# Revit family: O5DMA
name_source: partatom
category: Mechanical Equipment
units: mm (PartAtom-declared; Revit-internal decimal feet)

## family parameters
Always vertical = Yes
Cut with Voids When Loaded = No
OmniClass Number = 23.40.40.11.17
OmniClass Title = Refrigerated Cases
Part Type = Normal
Room Calculation Point = No
Round Connector Dimension = Use Radius
Shared = No
Work Plane-Based = Yes

## types (4) — shared parameters
24" Shelf = Yes
BOTTOM ELECTRICAL = Yes
BOTTOM REFRIGERATION PIPING = Yes
Certifications = NSF 7, UL471, CSA
Condensing  Data Volts = 208 V
Condensing Data  Phase = 1
Condensing Frequency (Hz) = 60 Hz
DATE = 05/20/2016
DESIGNERS NAME = SHIDDRAMESH
DRAIN PIPING = Yes
Default Elevation = 48"
Defrosts Per Day = 6
Description = Multi-Deck Merchandiser
Discharge Air (°F) = 31 °F
Discharge Air Velocity (FPM) = 200 FPM
EQUIPMENT DESCRIPTION = Multi-Deck Merchandiser
EQUIPMENT MARK = O5DMA-NRG
GLASS = Glass
Height = 101 5/8"
Item Description = Multi-Deck Merchandiser
LF STD END = Yes
Legend Number = O5DMA-NRG
Manufacturer = HILL PHOENIX
Model = O5DMA-NRG
PAINTED METAL UPPER SHELF = PAINTED SHELVES
REAR REFRIGERATION PIPING = Yes
RT STD END = Yes
Refrigerant = R404A
Suction Pressure @ Case Outlet (psig) = 58.00 psi
Superheat Set Point @ Bulb (°F) = 6-8  °F
System Data Phase = 1
System Data Volts = 208 V
Systems Frequency = 60 Hz
Systems Wire = 3 wire + ground
TOP ELECTRICAL = Yes
TOP REFRIGERATION PIPING = Yes
Timed-Off Defrost Fail-Safe (Min) = 45 (min)
Timed-Off Defrost Termination Temp = 42 °F
URL = http://www.hillphoenix.com
Width = 43 1/4"

## per-type parameters (varying)
| type | CENTER LINE | Condensed Horsepower | DRAIN LINE | Drain Pump Amps | Drain Pump Watts | Evaporator Pan Heater  Amps | Evaporator Pan Heater  Watts | High Efficiency Amps | High Efficiency Watts | Lbs. of Refrigerant | Length | Length of Cases | Locked Rotor (LRA) Amps | Maximum Lights Amps | Maximum Lights Watts | Number of Fans | Refgn | Running Load (RLA) Amps | Systems Maximum Overcurrent Protection | Systems Minimum Circuit Amps |
| 4' | 24" | 1 | 36" | 1 A | 47 W | 7 A | 1500 W | 0 A | 28 W | 4.5 | 48" | 48" | 46 A | 0 A | 35 W | 2 | 22 1/2" | 10 A | 25 A | 21 A |
| 6' | 36" | 1 - 3/4 | 36" | 1 A | 47 W | 7 A | 1500 W | 0 A | 28 W | 5.2 | 72" | 0" | 55 A | 0 A | 56 W | 2 | 28 5/8" | 13 A | 35 A | 25 A |
| 8' | 48" | 2 | 48" | 1 A | 47 W | 7 A | 1500 W | 0 A | 35 W | 5.2 | 96" | 0" | 56 A | 1 A | 71 W | 2 | 28 5/8" | 12 A | 35 A | 25 A |
| 12' | 72" |  | 72" | 0 A | 0 W | 0 A | 0 W | 1 A | 70 W | 8.1 | 144" | 0" | 75 A | 2 A | 195 W | 4 | 28 5/8" | 18 A | 40 A | 25 A |

## geometry (parser evidence)
native form markers: Blend x10, Sweep x2
no freeform markers — native parametric forms only
